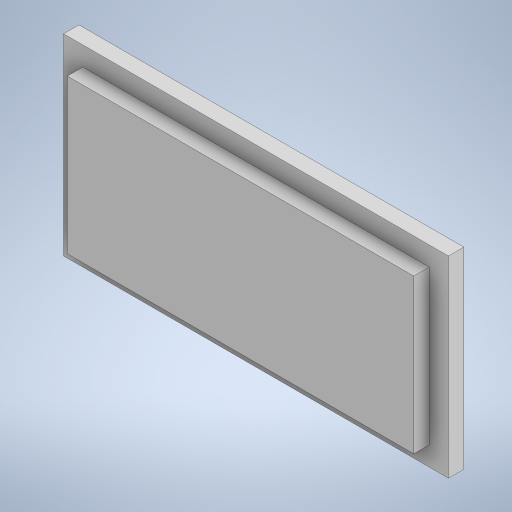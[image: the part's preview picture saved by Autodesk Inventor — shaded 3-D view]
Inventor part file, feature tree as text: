
AUTODESK INVENTOR PART (.ipt)
format: ipt  version: 2024.2 (Build 282272000, 272)  size: 249,344 bytes
history: native  units: mm
features: extrude x2, sketch x2
ambient origin geometry x8: Origin, YZ Plane, XZ Plane, XY Plane, X Axis, Y Axis, Z Axis, Center Point
bodies: Solid1 (feature_tree)
feature tree (4):
  extrude  "Extrusion1"  Depth=25.0mm
  extrude  "Extrusion2"  Depth=45.0mm
  sketch  "Sketch1"  dims[d0=50.0mm d1=25.0mm]
  sketch  "Sketch2"  dims[d2=2.0mm d3=0.0mm d4=45.0mm d5=20.0mm d6=2.5mm d7=2.5mm d8=2.0mm d9=0.0mm]
